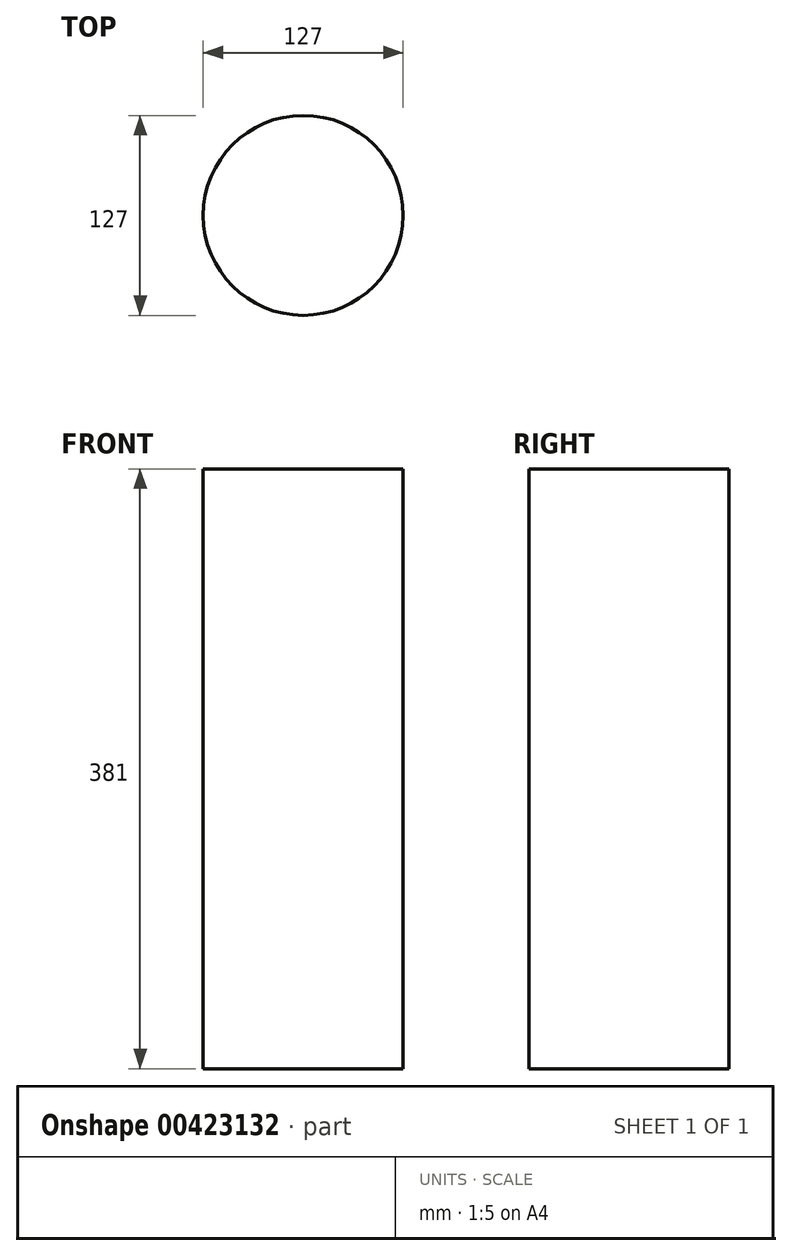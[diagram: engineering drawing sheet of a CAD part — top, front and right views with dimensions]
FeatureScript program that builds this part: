
annotation { "Feature Type Name" : "Feature", "Feature Type Description" : "" }
export const myFeature = defineFeature(function(context is Context, id is Id, definition is map)
    precondition{}
    {
        {
            var Q0;
            Q0=qCreatedBy(makeId("Top.planeOp"),FACE);
            var sketch = newSketch(context, id + "F0", { "sketchPlane" : qUnion([Q0])});
            skCircle(sketch, "E0", {"center": v(0, 0) * mm, "radius": 63.5 * mm});
            skSolve(sketch);
        }
        {
            var Q0;
            Q0=makeQuery(id+"F0.imprint","IMPRINT",FACE,{"disambiguationData":[TD([[makeQuery(id+"F0.imprint","IMPRINT",EDGE,{"derivedFrom":sQuery(id+"F0.wireOp",EDGE,"E0")}),1.0]])]});
            extrude(context, id + "F1", {"entities" : qUnion([Q0]), "depth" : 381 * mm, "offsetDistance" : 25.4 * mm});
        }
    });
